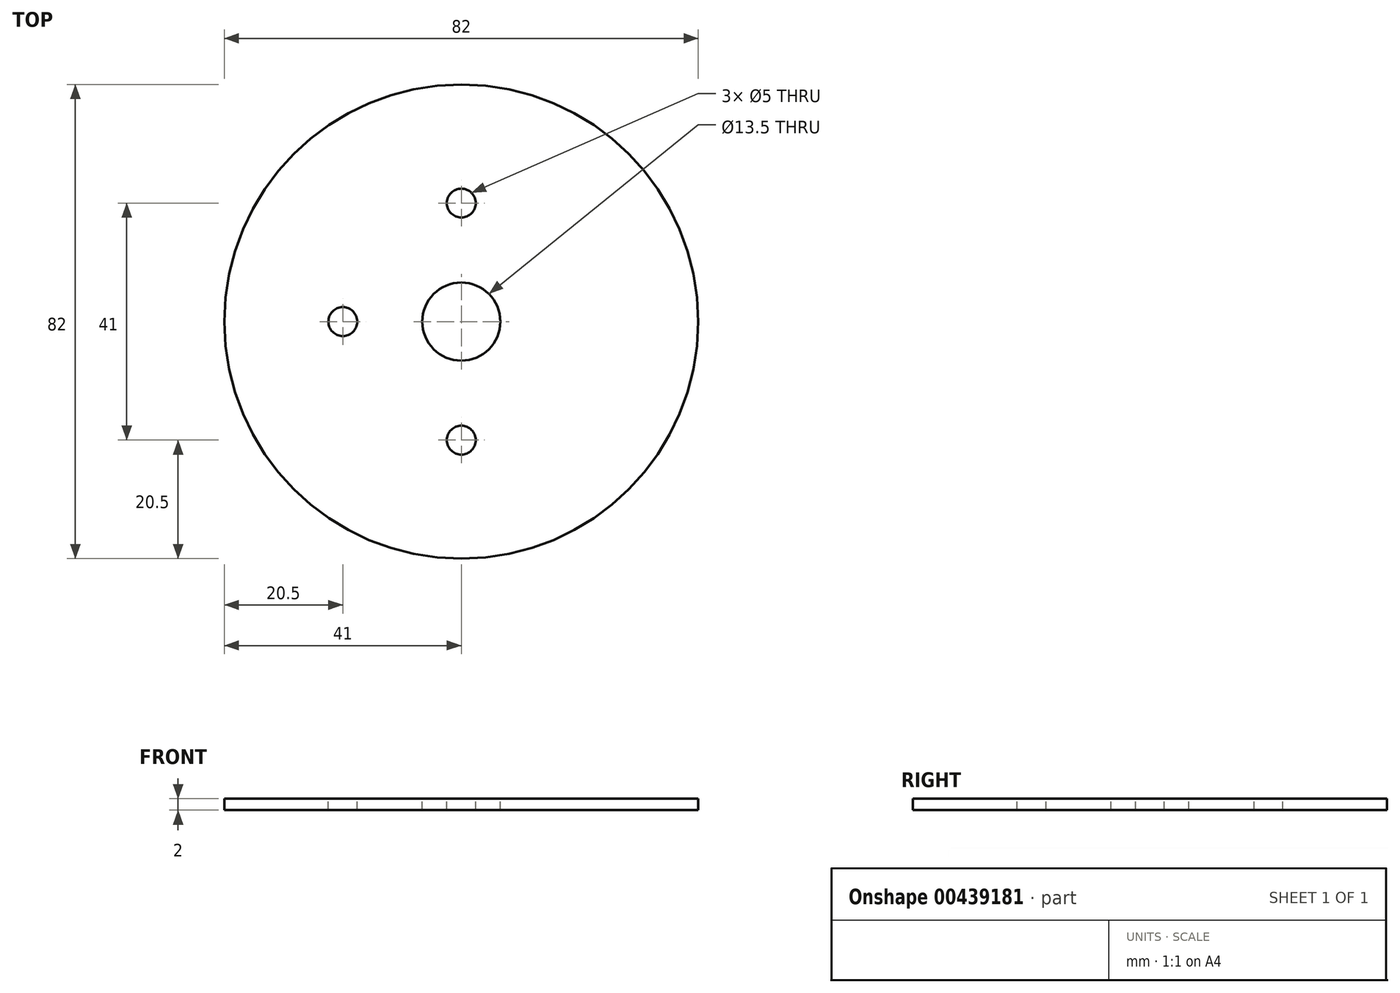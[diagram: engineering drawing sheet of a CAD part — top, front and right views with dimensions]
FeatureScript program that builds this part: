
annotation { "Feature Type Name" : "Feature", "Feature Type Description" : "" }
export const myFeature = defineFeature(function(context is Context, id is Id, definition is map)
    precondition{}
    {
        {
            var Q0;
            Q0=qCreatedBy(makeId("Top.planeOp"),FACE);
            var sketch = newSketch(context, id + "F0", { "sketchPlane" : qUnion([Q0])});
            skCircle(sketch, "E0", {"center": v(0, 0) * mm, "radius": 41 * mm});
            skSolve(sketch);
        }
        {
            var Q0;
            Q0 = qSketchRegion(id + "F0", true);
            extrude(context, id + "F1", {"entities" : qUnion([Q0]), "depth" : 2 * mm});
        }
        {
            var Q0;
            Q0=makeQuery(id+"F1.opExtrude","CAP_FACE",FACE,{"disambiguationData":[OSD([sQuery(id+"F0.wireOp",EDGE,"E0")])],"isStart":false});
            var sketch = newSketch(context, id + "F2", { "sketchPlane" : qUnion([Q0])});
            skLineSegment(sketch, "E1", {"start": v(0, 0) * mm, "end": v(0, 41) * mm});
            skLineSegment(sketch, "E2", {"start": v(0, 0) * mm, "end": v(0, -41) * mm});
            skLineSegment(sketch, "E3", {"start": v(0, 0) * mm, "end": v(-41, 0) * mm});
            skLineSegment(sketch, "E4", {"start": v(0, 0) * mm, "end": v(41, 0) * mm});
            skPoint(sketch, "E5", {"position": v(-20.5, 0) * mm});
            skPoint(sketch, "E6", {"position": v(0, 20.5) * mm});
            skPoint(sketch, "E7", {"position": v(20.5, 0) * mm});
            skPoint(sketch, "E8", {"position": v(0, -20.5) * mm});
            skLineSegment(sketch, "E9", {"start": v(-20.5, 0) * mm, "end": v(0, 20.5) * mm});
            skLineSegment(sketch, "E10", {"start": v(0, 20.5) * mm, "end": v(20.5, 0) * mm});
            skLineSegment(sketch, "E11", {"start": v(0, -20.5) * mm, "end": v(20.5, 0) * mm});
            skLineSegment(sketch, "E12", {"start": v(-20.5, 0) * mm, "end": v(0, -20.5) * mm});
            skPoint(sketch, "E13", {"position": v(-10.25, 10.25) * mm});
            skPoint(sketch, "E14", {"position": v(-10.25, -10.25) * mm});
            skPoint(sketch, "E15", {"position": v(10.25, -10.25) * mm});
            skPoint(sketch, "E16", {"position": v(10.25, 10.25) * mm});
            skLineSegment(sketch, "E17", {"start": v(0, 0) * mm, "end": v(-29, 29) * mm});
            skLineSegment(sketch, "E18", {"start": v(0, 0) * mm, "end": v(-29, -29) * mm});
            skLineSegment(sketch, "E19", {"start": v(0, 0) * mm, "end": v(29, -29) * mm});
            skLineSegment(sketch, "E20", {"start": v(0, 0) * mm, "end": v(29, 29) * mm});
            skCircle(sketch, "E21", {"center": v(0, -20.5) * mm, "radius": 2.5 * mm});
            skCircle(sketch, "E22", {"center": v(0, 20.5) * mm, "radius": 2.5 * mm});
            skCircle(sketch, "E23", {"center": v(-20.5, 0) * mm, "radius": 2.5 * mm});
            skLineSegment(sketch, "E24", {"start": v(10.12, 0) * mm, "end": v(10.12, -6.25) * mm});
            skLineSegment(sketch, "E25", {"start": v(10.12, 0) * mm, "end": v(10.12, 6.25) * mm});
            skLineSegment(sketch, "E26", {"start": v(14.25, -6.25) * mm, "end": v(10.12, -6.25) * mm});
            skLineSegment(sketch, "E27", {"start": v(10.12, 6.25) * mm, "end": v(14.25, 6.25) * mm});
            skLineSegment(sketch, "E28", {"start": v(10.12, -6.25) * mm, "end": v(0, 0) * mm});
            skLineSegment(sketch, "E29", {"start": v(10.12, 6.25) * mm, "end": v(0, 0) * mm});
            skCircle(sketch, "E30", {"center": v(0, 0) * mm, "radius": 6.75 * mm});
            skLineSegment(sketch, "E31", {"start": v(41, 0) * mm, "end": v(31, 0) * mm});
            skLineSegment(sketch, "E32", {"start": v(31, 0) * mm, "end": v(31, 26.83) * mm});
            skLineSegment(sketch, "E33", {"start": v(31, 0) * mm, "end": v(31, -26.83) * mm});
            skSolve(sketch);
        }
        {
            var Q0;
            {var subQ1=sQuery(id+"F2.wireOp",EDGE,"E3");var subQ3=sQuery(id+"F2.wireOp",EDGE,"E23");var subQ4=makeQuery(id+"F2.imprint","INTERSECT",VERTEX,{"disambiguationData":[OD(1.0)],"derivedFrom":[subQ1,subQ3]});Q0=makeQuery(id+"F2.imprint","IMPRINT",FACE,{"disambiguationData":[TD([[makeQuery(id+"F2.imprint","IMPRINT",EDGE,{"disambiguationData":[TD([[subQ4,1.0]])],"derivedFrom":subQ3}),1.0]])]});}
            var Q1;
            {var subQ1=sQuery(id+"F2.wireOp",EDGE,"E3");var subQ3=sQuery(id+"F2.wireOp",EDGE,"E23");var subQ4=makeQuery(id+"F2.imprint","INTERSECT",VERTEX,{"disambiguationData":[OD(1.0)],"derivedFrom":[subQ1,subQ3]});Q1=makeQuery(id+"F2.imprint","IMPRINT",FACE,{"disambiguationData":[TD([[makeQuery(id+"F2.imprint","IMPRINT",EDGE,{"disambiguationData":[TD([[subQ4,-1.0]])],"derivedFrom":subQ3}),1.0]])]});}
            var Q2;
            {var subQ1=sQuery(id+"F2.wireOp",EDGE,"E3");var subQ3=sQuery(id+"F2.wireOp",EDGE,"E23");var subQ4=makeQuery(id+"F2.imprint","INTERSECT",VERTEX,{"disambiguationData":[OD(0.0)],"derivedFrom":[subQ1,subQ3]});Q2=makeQuery(id+"F2.imprint","IMPRINT",FACE,{"disambiguationData":[TD([[makeQuery(id+"F2.imprint","IMPRINT",EDGE,{"disambiguationData":[TD([[subQ4,1.0]])],"derivedFrom":subQ3}),1.0]])]});}
            var Q3;
            {var subQ1=sQuery(id+"F2.wireOp",EDGE,"E3");var subQ3=sQuery(id+"F2.wireOp",EDGE,"E23");var subQ4=makeQuery(id+"F2.imprint","INTERSECT",VERTEX,{"disambiguationData":[OD(0.0)],"derivedFrom":[subQ1,subQ3]});Q3=makeQuery(id+"F2.imprint","IMPRINT",FACE,{"disambiguationData":[TD([[makeQuery(id+"F2.imprint","IMPRINT",EDGE,{"disambiguationData":[TD([[subQ4,-1.0]])],"derivedFrom":subQ3}),1.0]])]});}
            var Q4;
            {var subQ1=sQuery(id+"F2.wireOp",EDGE,"E1");var subQ3=sQuery(id+"F2.wireOp",EDGE,"E22");var subQ4=makeQuery(id+"F2.imprint","INTERSECT",VERTEX,{"disambiguationData":[OD(1.0)],"derivedFrom":[subQ1,subQ3]});Q4=makeQuery(id+"F2.imprint","IMPRINT",FACE,{"disambiguationData":[TD([[makeQuery(id+"F2.imprint","IMPRINT",EDGE,{"disambiguationData":[TD([[subQ4,-1.0]])],"derivedFrom":subQ3}),1.0]])]});}
            var Q5;
            {var subQ1=sQuery(id+"F2.wireOp",EDGE,"E1");var subQ3=sQuery(id+"F2.wireOp",EDGE,"E22");var subQ4=makeQuery(id+"F2.imprint","INTERSECT",VERTEX,{"disambiguationData":[OD(0.0)],"derivedFrom":[subQ1,subQ3]});Q5=makeQuery(id+"F2.imprint","IMPRINT",FACE,{"disambiguationData":[TD([[makeQuery(id+"F2.imprint","IMPRINT",EDGE,{"disambiguationData":[TD([[subQ4,1.0]])],"derivedFrom":subQ3}),1.0]])]});}
            var Q6;
            {var subQ1=sQuery(id+"F2.wireOp",EDGE,"E1");var subQ3=sQuery(id+"F2.wireOp",EDGE,"E22");var subQ4=makeQuery(id+"F2.imprint","INTERSECT",VERTEX,{"disambiguationData":[OD(0.0)],"derivedFrom":[subQ1,subQ3]});Q6=makeQuery(id+"F2.imprint","IMPRINT",FACE,{"disambiguationData":[TD([[makeQuery(id+"F2.imprint","IMPRINT",EDGE,{"disambiguationData":[TD([[subQ4,-1.0]])],"derivedFrom":subQ3}),1.0]])]});}
            var Q7;
            {var subQ1=sQuery(id+"F2.wireOp",EDGE,"E1");var subQ3=sQuery(id+"F2.wireOp",EDGE,"E22");var subQ4=makeQuery(id+"F2.imprint","INTERSECT",VERTEX,{"disambiguationData":[OD(1.0)],"derivedFrom":[subQ1,subQ3]});Q7=makeQuery(id+"F2.imprint","IMPRINT",FACE,{"disambiguationData":[TD([[makeQuery(id+"F2.imprint","IMPRINT",EDGE,{"disambiguationData":[TD([[subQ4,1.0]])],"derivedFrom":subQ3}),1.0]])]});}
            var Q8;
            {var subQ1=sQuery(id+"F2.wireOp",EDGE,"E1");var subQ3=sQuery(id+"F2.wireOp",EDGE,"E30");var subQ4=makeQuery(id+"F2.imprint","INTERSECT",VERTEX,{"derivedFrom":[subQ1,subQ3]});Q8=makeQuery(id+"F2.imprint","IMPRINT",FACE,{"disambiguationData":[TD([[makeQuery(id+"F2.imprint","IMPRINT",EDGE,{"disambiguationData":[TD([[subQ4,-1.0]])],"derivedFrom":subQ3}),1.0]])]});}
            var Q9;
            {var subQ1=sQuery(id+"F2.wireOp",EDGE,"E3");var subQ3=sQuery(id+"F2.wireOp",EDGE,"E30");var subQ4=makeQuery(id+"F2.imprint","INTERSECT",VERTEX,{"derivedFrom":[subQ1,subQ3]});Q9=makeQuery(id+"F2.imprint","IMPRINT",FACE,{"disambiguationData":[TD([[makeQuery(id+"F2.imprint","IMPRINT",EDGE,{"disambiguationData":[TD([[subQ4,1.0]])],"derivedFrom":subQ3}),1.0]])]});}
            var Q10;
            {var subQ1=sQuery(id+"F2.wireOp",EDGE,"E3");var subQ3=sQuery(id+"F2.wireOp",EDGE,"E30");var subQ4=makeQuery(id+"F2.imprint","INTERSECT",VERTEX,{"derivedFrom":[subQ1,subQ3]});Q10=makeQuery(id+"F2.imprint","IMPRINT",FACE,{"disambiguationData":[TD([[makeQuery(id+"F2.imprint","IMPRINT",EDGE,{"disambiguationData":[TD([[subQ4,-1.0]])],"derivedFrom":subQ3}),1.0]])]});}
            var Q11;
            {var subQ1=sQuery(id+"F2.wireOp",EDGE,"E2");var subQ3=sQuery(id+"F2.wireOp",EDGE,"E30");var subQ4=makeQuery(id+"F2.imprint","INTERSECT",VERTEX,{"derivedFrom":[subQ1,subQ3]});Q11=makeQuery(id+"F2.imprint","IMPRINT",FACE,{"disambiguationData":[TD([[makeQuery(id+"F2.imprint","IMPRINT",EDGE,{"disambiguationData":[TD([[subQ4,1.0]])],"derivedFrom":subQ3}),1.0]])]});}
            var Q12;
            {var subQ1=sQuery(id+"F2.wireOp",EDGE,"E2");var subQ3=sQuery(id+"F2.wireOp",EDGE,"E30");var subQ4=makeQuery(id+"F2.imprint","INTERSECT",VERTEX,{"derivedFrom":[subQ1,subQ3]});Q12=makeQuery(id+"F2.imprint","IMPRINT",FACE,{"disambiguationData":[TD([[makeQuery(id+"F2.imprint","IMPRINT",EDGE,{"disambiguationData":[TD([[subQ4,-1.0]])],"derivedFrom":subQ3}),1.0]])]});}
            var Q13;
            {var subQ1=sQuery(id+"F2.wireOp",EDGE,"E4");var subQ3=sQuery(id+"F2.wireOp",EDGE,"E30");var subQ4=makeQuery(id+"F2.imprint","INTERSECT",VERTEX,{"derivedFrom":[subQ1,subQ3]});Q13=makeQuery(id+"F2.imprint","IMPRINT",FACE,{"disambiguationData":[TD([[makeQuery(id+"F2.imprint","IMPRINT",EDGE,{"disambiguationData":[TD([[subQ4,1.0]])],"derivedFrom":subQ3}),1.0]])]});}
            var Q14;
            {var subQ1=sQuery(id+"F2.wireOp",EDGE,"E4");var subQ3=sQuery(id+"F2.wireOp",EDGE,"E30");var subQ4=makeQuery(id+"F2.imprint","INTERSECT",VERTEX,{"derivedFrom":[subQ1,subQ3]});Q14=makeQuery(id+"F2.imprint","IMPRINT",FACE,{"disambiguationData":[TD([[makeQuery(id+"F2.imprint","IMPRINT",EDGE,{"disambiguationData":[TD([[subQ4,-1.0]])],"derivedFrom":subQ3}),1.0]])]});}
            var Q15;
            {var subQ1=sQuery(id+"F2.wireOp",EDGE,"E1");var subQ3=sQuery(id+"F2.wireOp",EDGE,"E30");var subQ4=makeQuery(id+"F2.imprint","INTERSECT",VERTEX,{"derivedFrom":[subQ1,subQ3]});Q15=makeQuery(id+"F2.imprint","IMPRINT",FACE,{"disambiguationData":[TD([[makeQuery(id+"F2.imprint","IMPRINT",EDGE,{"disambiguationData":[TD([[subQ4,1.0]])],"derivedFrom":subQ3}),1.0]])]});}
            var Q16;
            {var subQ1=sQuery(id+"F2.wireOp",EDGE,"E19");var subQ3=sQuery(id+"F2.wireOp",EDGE,"E30");var subQ4=makeQuery(id+"F2.imprint","INTERSECT",VERTEX,{"derivedFrom":[subQ1,subQ3]});Q16=makeQuery(id+"F2.imprint","IMPRINT",FACE,{"disambiguationData":[TD([[makeQuery(id+"F2.imprint","IMPRINT",EDGE,{"disambiguationData":[TD([[subQ4,-1.0]])],"derivedFrom":subQ3}),1.0]])]});}
            var Q17;
            {var subQ1=sQuery(id+"F2.wireOp",EDGE,"E20");var subQ3=sQuery(id+"F2.wireOp",EDGE,"E30");var subQ4=makeQuery(id+"F2.imprint","INTERSECT",VERTEX,{"derivedFrom":[subQ1,subQ3]});Q17=makeQuery(id+"F2.imprint","IMPRINT",FACE,{"disambiguationData":[TD([[makeQuery(id+"F2.imprint","IMPRINT",EDGE,{"disambiguationData":[TD([[subQ4,1.0]])],"derivedFrom":subQ3}),1.0]])]});}
            var Q18;
            {var subQ1=sQuery(id+"F2.wireOp",EDGE,"E2");var subQ3=sQuery(id+"F2.wireOp",EDGE,"E21");var subQ4=makeQuery(id+"F2.imprint","INTERSECT",VERTEX,{"disambiguationData":[OD(1.0)],"derivedFrom":[subQ1,subQ3]});Q18=makeQuery(id+"F2.imprint","IMPRINT",FACE,{"disambiguationData":[TD([[makeQuery(id+"F2.imprint","IMPRINT",EDGE,{"disambiguationData":[TD([[subQ4,1.0]])],"derivedFrom":subQ3}),1.0]])]});}
            var Q19;
            {var subQ1=sQuery(id+"F2.wireOp",EDGE,"E2");var subQ3=sQuery(id+"F2.wireOp",EDGE,"E21");var subQ4=makeQuery(id+"F2.imprint","INTERSECT",VERTEX,{"disambiguationData":[OD(0.0)],"derivedFrom":[subQ1,subQ3]});Q19=makeQuery(id+"F2.imprint","IMPRINT",FACE,{"disambiguationData":[TD([[makeQuery(id+"F2.imprint","IMPRINT",EDGE,{"disambiguationData":[TD([[subQ4,1.0]])],"derivedFrom":subQ3}),1.0]])]});}
            var Q20;
            {var subQ1=sQuery(id+"F2.wireOp",EDGE,"E2");var subQ3=sQuery(id+"F2.wireOp",EDGE,"E21");var subQ4=makeQuery(id+"F2.imprint","INTERSECT",VERTEX,{"disambiguationData":[OD(0.0)],"derivedFrom":[subQ1,subQ3]});Q20=makeQuery(id+"F2.imprint","IMPRINT",FACE,{"disambiguationData":[TD([[makeQuery(id+"F2.imprint","IMPRINT",EDGE,{"disambiguationData":[TD([[subQ4,-1.0]])],"derivedFrom":subQ3}),1.0]])]});}
            var Q21;
            {var subQ1=sQuery(id+"F2.wireOp",EDGE,"E2");var subQ3=sQuery(id+"F2.wireOp",EDGE,"E21");var subQ4=makeQuery(id+"F2.imprint","INTERSECT",VERTEX,{"disambiguationData":[OD(1.0)],"derivedFrom":[subQ1,subQ3]});Q21=makeQuery(id+"F2.imprint","IMPRINT",FACE,{"disambiguationData":[TD([[makeQuery(id+"F2.imprint","IMPRINT",EDGE,{"disambiguationData":[TD([[subQ4,-1.0]])],"derivedFrom":subQ3}),1.0]])]});}
            var Q22;
            {var subQ0=sQuery(id+"F2.wireOp",EDGE,"E31");Q22=makeQuery(id+"F2.imprint","IMPRINT",FACE,{"disambiguationData":[TD([[makeQuery(id+"F2.imprint","IMPRINT",EDGE,{"derivedFrom":subQ0}),1.0]])]});}
            var Q23;
            {var subQ0=sQuery(id+"F2.wireOp",EDGE,"E31");Q23=makeQuery(id+"F2.imprint","IMPRINT",FACE,{"disambiguationData":[TD([[makeQuery(id+"F2.imprint","IMPRINT",EDGE,{"derivedFrom":subQ0}),-1.0]])]});}
            extrude(context, id + "F3", {"entities" : qUnion([Q0, Q1, Q2, Q3, Q4, Q5, Q6, Q7, Q8, Q9, Q10, Q11, Q12, Q13, Q14, Q15, Q16, Q17, Q18, Q19, Q20, Q21, Q22, Q23]), "operationType" : NewBodyOperationType.REMOVE, "endBound" : BoundingType.THROUGH_ALL, "oppositeDirection" : true, "depth" : 25 * mm});
        }
    });
